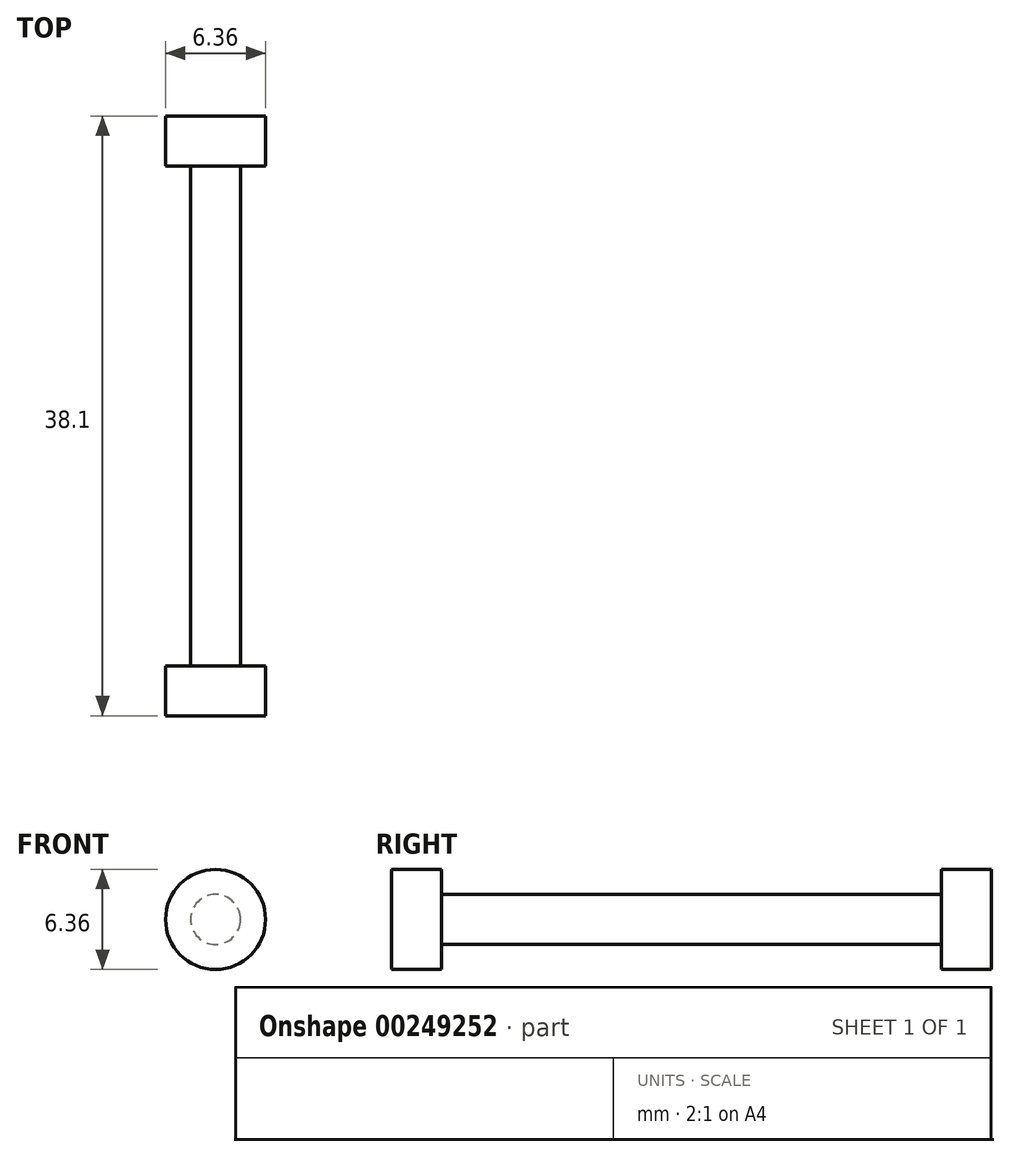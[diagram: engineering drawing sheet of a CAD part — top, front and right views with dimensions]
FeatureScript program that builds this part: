
annotation { "Feature Type Name" : "Feature", "Feature Type Description" : "" }
export const myFeature = defineFeature(function(context is Context, id is Id, definition is map)
    precondition{}
    {
        {
            var Q0;
            Q0=qCreatedBy(makeId("Front.planeOp"),FACE);
            var sketch = newSketch(context, id + "F0", { "sketchPlane" : qUnion([Q0])});
            skCircle(sketch, "E0", {"center": v(0, 0) * mm, "radius": 3.18 * mm});
            skSolve(sketch);
        }
        {
            var Q0;
            Q0=makeQuery(id+"F0.imprint","IMPRINT",FACE,{"disambiguationData":[TD([[makeQuery(id+"F0.imprint","IMPRINT",EDGE,{"derivedFrom":sQuery(id+"F0.wireOp",EDGE,"E0")}),1.0]])]});
            extrude(context, id + "F1", {"entities" : qUnion([Q0]), "depth" : 3.17 * mm});
        }
        {
            var Q0;
            Q0=makeQuery(id+"F1.opExtrude","CAP_FACE",FACE,{"disambiguationData":[OSD([sQuery(id+"F0.wireOp",EDGE,"E0")])],"isStart":false});
            var sketch = newSketch(context, id + "F2", { "sketchPlane" : qUnion([Q0])});
            skCircle(sketch, "E1", {"center": v(0, 0) * mm, "radius": 1.59 * mm});
            skSolve(sketch);
        }
        {
            var Q0;
            Q0=makeQuery(id+"F2.imprint","IMPRINT",FACE,{"disambiguationData":[TD([[makeQuery(id+"F2.imprint","IMPRINT",EDGE,{"derivedFrom":sQuery(id+"F2.wireOp",EDGE,"E1")}),1.0]])]});
            extrude(context, id + "F3", {"entities" : qUnion([Q0]), "operationType" : NewBodyOperationType.ADD, "depth" : 31.75 * mm});
        }
        {
            var Q0;
            Q0=makeQuery(id+"F3.opExtrude","CAP_FACE",FACE,{"disambiguationData":[OSD([sQuery(id+"F2.wireOp",EDGE,"E1")])],"isStart":false});
            var sketch = newSketch(context, id + "F4", { "sketchPlane" : qUnion([Q0])});
            skCircle(sketch, "E2", {"center": v(0, 0) * mm, "radius": 3.18 * mm});
            skSolve(sketch);
        }
        {
            var Q0;
            Q0=makeQuery(id+"F4.imprint","IMPRINT",FACE,{"disambiguationData":[TD([[makeQuery(id+"F4.imprint","IMPRINT",EDGE,{"derivedFrom":sQuery(id+"F4.wireOp",EDGE,"E2")}),1.0]])]});
            var Q1;
            Q1=makeQuery(id+"F4.imprint","IMPRINT",FACE,{"disambiguationData":[TD([[makeQuery(id+"F4.imprint","IMPRINT",EDGE,{"derivedFrom":makeQuery(id+"F3.opExtrude","CAP_EDGE",EDGE,{"disambiguationData":[OSD([sQuery(id+"F2.wireOp",EDGE,"E1")])],"isStart":false})}),1.0]])]});
            extrude(context, id + "F5", {"entities" : qUnion([Q0, Q1]), "operationType" : NewBodyOperationType.ADD, "depth" : 3.17 * mm});
        }
    });
